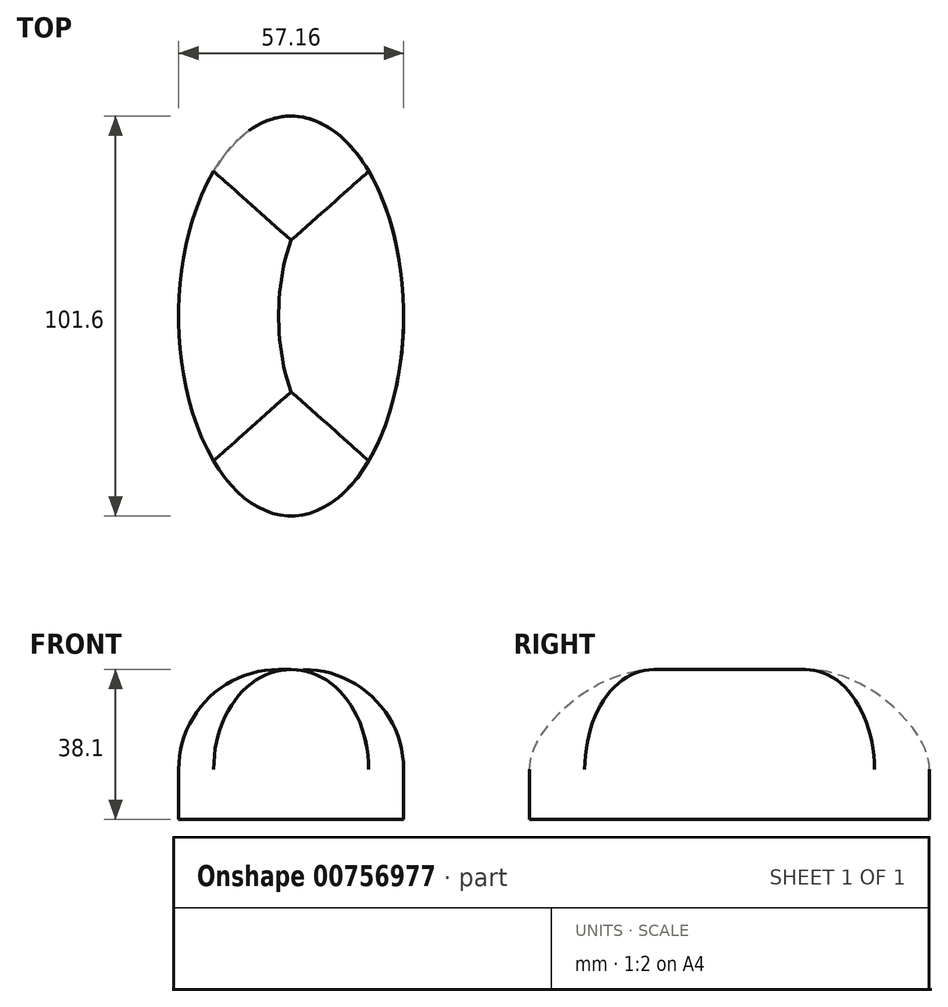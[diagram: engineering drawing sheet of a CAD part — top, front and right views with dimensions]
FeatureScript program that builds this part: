
annotation { "Feature Type Name" : "Feature", "Feature Type Description" : "" }
export const myFeature = defineFeature(function(context is Context, id is Id, definition is map)
    precondition{}
    {
        {
            var Q0;
            Q0=qCreatedBy(makeId("Top.planeOp"),FACE);
            var sketch = newSketch(context, id + "F0", { "sketchPlane" : qUnion([Q0])});
            skEllipse(sketch, "E0", {"center": v(0, 0) * mm, "majorRadius": 50.8 * mm, "minorRadius": 28.58 * mm, "majorAxis": v(0, 1)});
            skSolve(sketch);
        }
        {
            var Q0;
            Q0=qSketchRegion(id+"F0",true);
            extrude(context, id + "F1", {"entities" : qUnion([Q0]), "depth" : 38.1 * mm});
        }
        {
            var Q0;
            Q0=makeQuery(id+"F1.opExtrude","CAP_EDGE",EDGE,{"disambiguationData":[OSD([sQuery(id+"F0.wireOp",EDGE,"E0")])],"isStart":false});
            fillet(context, id + "F2", {"entities" : qUnion([Q0]), "radius" : 25.4 * mm, "tangentPropagation" : true, "allowEdgeOverflow" : false});
        }
    });
